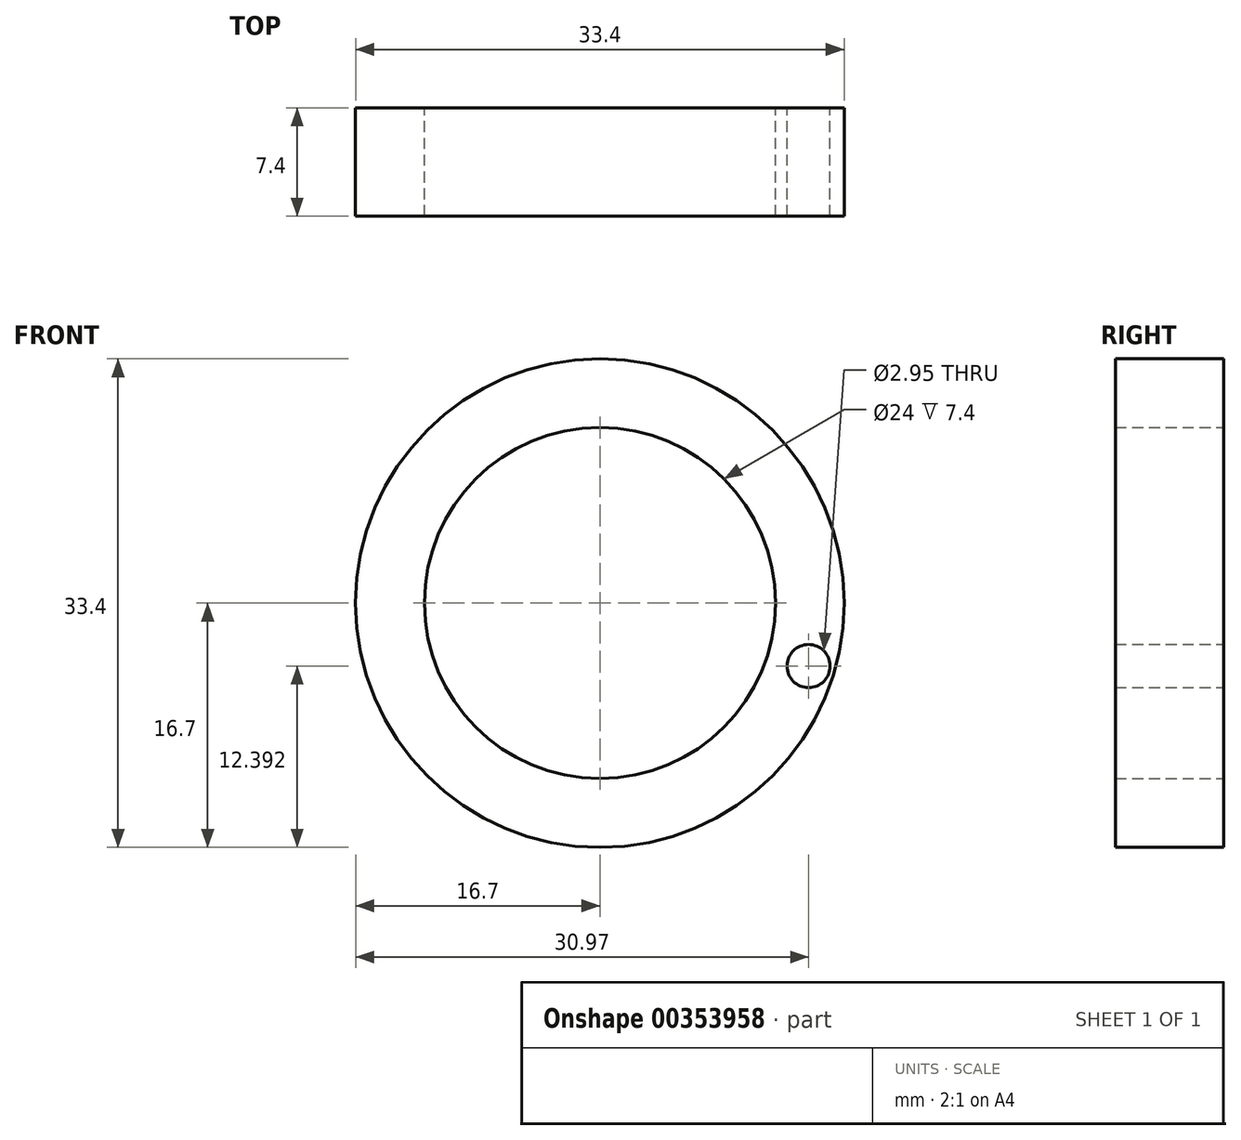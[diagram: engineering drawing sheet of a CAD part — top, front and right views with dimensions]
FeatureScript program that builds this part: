
annotation { "Feature Type Name" : "Feature", "Feature Type Description" : "" }
export const myFeature = defineFeature(function(context is Context, id is Id, definition is map)
    precondition{}
    {
        {
            var Q0;
            Q0=qCreatedBy(makeId("Front.planeOp"),FACE);
            var sketch = newSketch(context, id + "F0", { "sketchPlane" : qUnion([Q0])});
            skCircle(sketch, "E0", {"center": v(0, 0) * mm, "radius": 12 * mm});
            skCircle(sketch, "E1", {"center": v(0, 0) * mm, "radius": 16.7 * mm});
            skCircle(sketch, "E2", {"center": v(14.27, -4.3) * mm, "radius": 1.47 * mm});
            skSolve(sketch);
        }
        {
            var Q0;
            Q0=makeQuery(id+"F0.imprint","IMPRINT",FACE,{"disambiguationData":[TD([[makeQuery(id+"F0.imprint","IMPRINT",EDGE,{"derivedFrom":sQuery(id+"F0.wireOp",EDGE,"E0")}),-1.0]])]});
            extrude(context, id + "F1", {"entities" : qUnion([Q0]), "endBound" : BoundingType.SYMMETRIC, "depth" : 7.4 * mm});
        }
    });
